# Revit family: SHORT LARGE
name_source: partatom
category: Lighting Fixtures
units: mm (PartAtom-declared; Revit-internal decimal feet)

## family parameters
Cut with Voids When Loaded = No
Host = Face
Light Source = Yes
Maintain Annotation Orientation = Yes
Part Type = Normal
Room Calculation Point = No
Round Connector Dimension = Use Diameter
Shared = No

## types (8) — shared parameters
Color Filter = 16777215
Default Elevation = 1219 mm
Dimming Lamp Color Temperature Shift = <None>
Emit from Line Length = 610 mm
LuxLight_Alto = 118 mm
LuxLight_AltoAreaLuminosa = 30 mm  [stored 0.0984252 ft]
LuxLight_Amperios = 800
LuxLight_Diametro = 118 mm
LuxLight_DiametroAreaLuminosa = 95 mm
LuxLight_Watios = 30 W
Manufacturer = LUXLIGHT
Tilt Angle = 0.00°
zero-valued in all types: LuxLight_Ancho, LuxLight_AnchoAreaLuminosa, LuxLight_Largo, LuxLight_LargoAreaLuminosa, LuxLight_ProtuberanciaTecho

## per-type parameters (varying)
| type | LuxLight_Lumenes | LuxLight_Temperatura | Photometric Web File |
| LXT036L482 | 3461 lm | 2700 K | LXT036L482 .ies |
| LXT036L483 | 3665 lm | 3000 K | LXT036L483 .ies |
| LXT036L435 | 3288 lm | 3500 K | LXT036L435 .ies |
| LXT036L484 | 3878 lm | 4000 K | LXT036L484 .ies |
| LXT036L485 | 4072 lm | 5000 K | LXT036L485 .ies |
| LXT036L492 | 2715 lm | 2700 K | LXT036L492 .ies |
| LXT036L493 | 3102 lm | 3000 K | LXT036L493 .ies |
| LXT036L494 | 3490 lm | 4000 K | LXT036L494 .ies |

note: [stored X ft] marks values corroborated as IEEE doubles in the binary element streams (Revit-internal decimal feet)

## geometry (parser evidence)
native form markers: Sweep x2
no freeform markers — native parametric forms only
